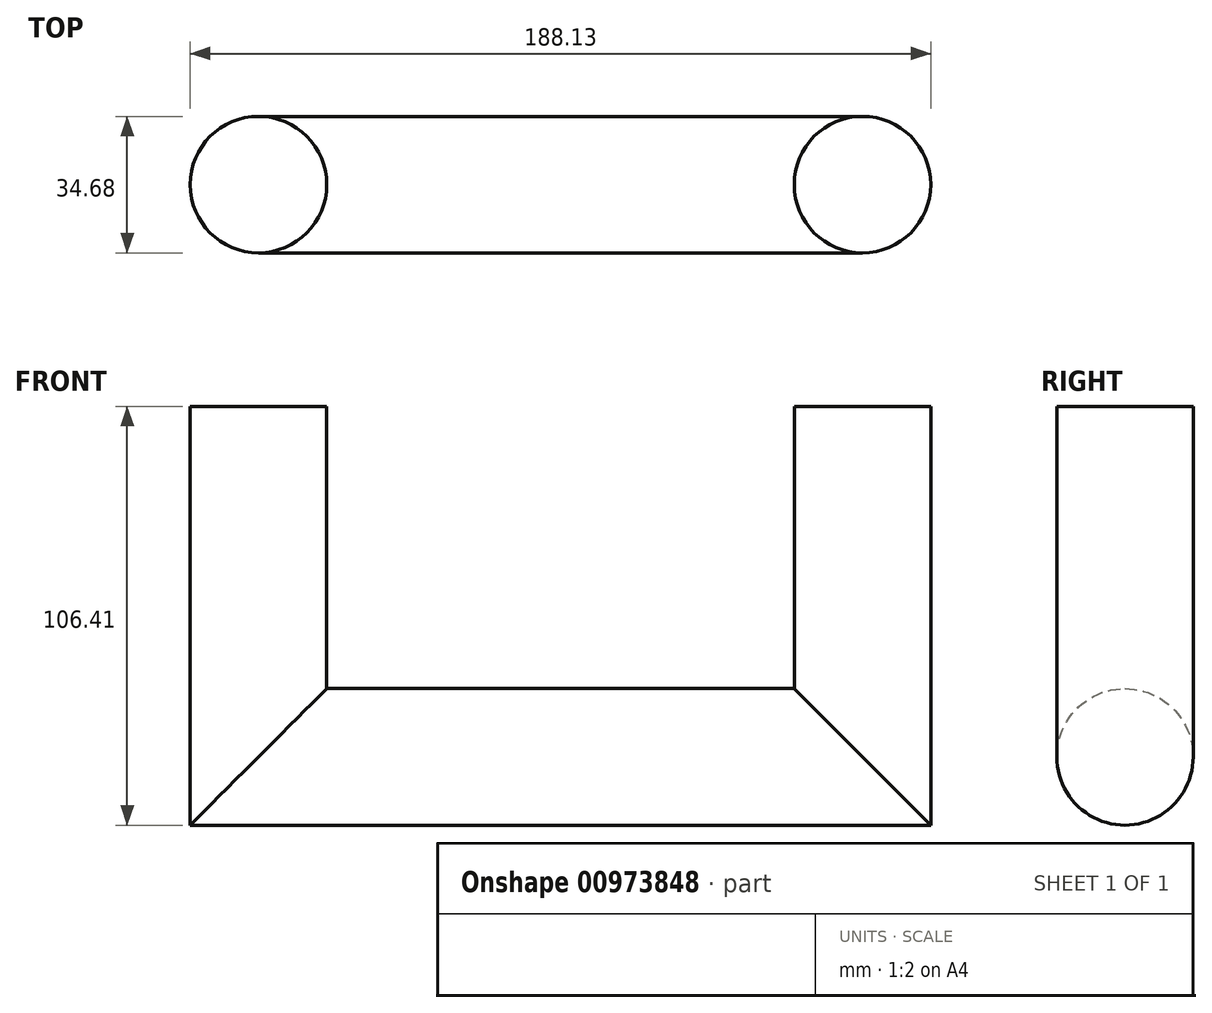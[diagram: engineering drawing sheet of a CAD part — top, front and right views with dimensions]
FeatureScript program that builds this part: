
annotation { "Feature Type Name" : "Feature", "Feature Type Description" : "" }
export const myFeature = defineFeature(function(context is Context, id is Id, definition is map)
    precondition{}
    {
        {
            var Q0;
            Q0=qCreatedBy(makeId("Top.planeOp"),FACE);
            var sketch = newSketch(context, id + "F0", { "sketchPlane" : qUnion([Q0])});
            skCircle(sketch, "E0", {"center": v(0, 0) * mm, "radius": 17.34 * mm});
            skSolve(sketch);
        }
        {
            var Q0;
            Q0=qCreatedBy(makeId("Front.planeOp"),FACE);
            var sketch = newSketch(context, id + "F1", { "sketchPlane" : qUnion([Q0])});
            skLineSegment(sketch, "E1.bottom", {"start": v(0, 0) * mm, "end": v(153.45, 0) * mm});
            skLineSegment(sketch, "E1.top", {"start": v(0, 89.07) * mm, "end": v(153.45, 89.07) * mm});
            skLineSegment(sketch, "E1.left", {"start": v(0, 0) * mm, "end": v(0, 89.07) * mm});
            skLineSegment(sketch, "E1.right", {"start": v(153.45, 0) * mm, "end": v(153.45, 89.07) * mm});
            skSolve(sketch);
        }
        {
            var Q0;
            Q0=makeQuery(id+"F0.imprint","IMPRINT",FACE,{"disambiguationData":[TD([[makeQuery(id+"F0.imprint","IMPRINT",EDGE,{"derivedFrom":sQuery(id+"F0.wireOp",EDGE,"E0")}),1.0]])]});
            var Q1;
            Q1=sQuery(id+"F1.wireOp",EDGE,"E1.bottom");
            var Q2;
            Q2=sQuery(id+"F1.wireOp",EDGE,"E1.left");
            var Q3;
            Q3=sQuery(id+"F1.wireOp",EDGE,"E1.right");
            sweep(context, id + "F2", {"profiles" : qUnion([Q0]), "path" : qUnion([Q1, Q2, Q3])});
        }
    });
